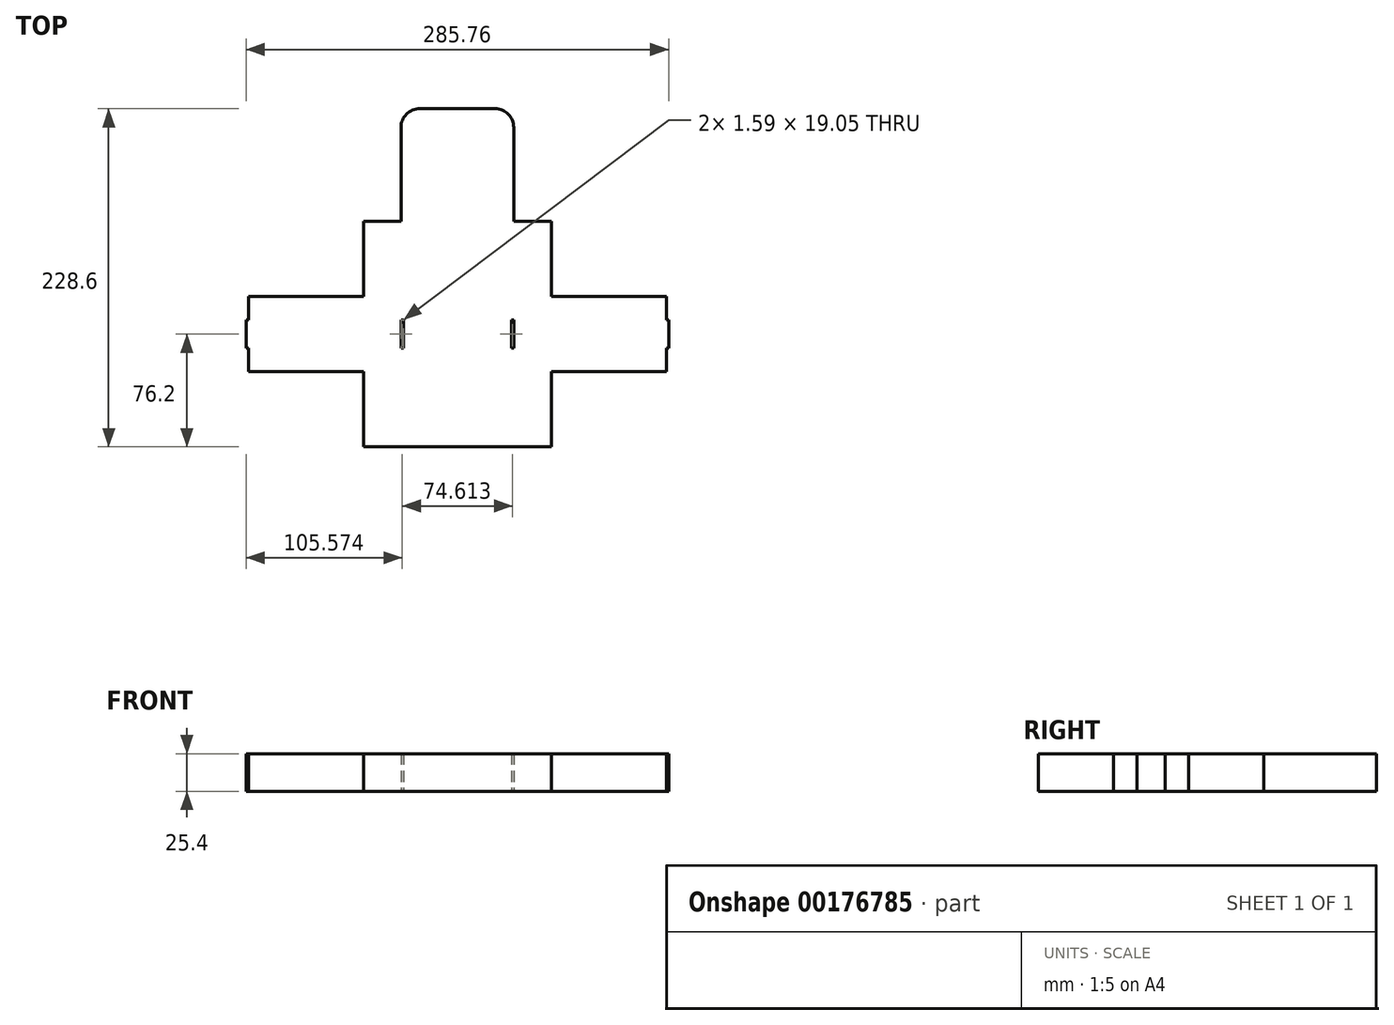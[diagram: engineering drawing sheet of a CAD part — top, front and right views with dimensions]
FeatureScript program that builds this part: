
annotation { "Feature Type Name" : "Feature", "Feature Type Description" : "" }
export const myFeature = defineFeature(function(context is Context, id is Id, definition is map)
    precondition{}
    {
        {
            var Q0;
            Q0=qCreatedBy(makeId("Top.planeOp"),FACE);
            var sketch = newSketch(context, id + "F0", { "sketchPlane" : qUnion([Q0])});
            skLineSegment(sketch, "E0.bottom", {"start": v(38.1, 25.4) * mm, "end": v(-38.1, 25.4) * mm});
            skLineSegment(sketch, "E0.top", {"start": v(38.1, -25.4) * mm, "end": v(-38.1, -25.4) * mm});
            skLineSegment(sketch, "E0.left", {"start": v(38.1, 25.4) * mm, "end": v(38.1, -25.4) * mm});
            skLineSegment(sketch, "E0.right", {"start": v(-38.1, 25.4) * mm, "end": v(-38.1, -25.4) * mm});
            skPoint(sketch, "E0.middle", {"position": v(0, 0) * mm});
            skLineSegment(sketch, "E1", {"start": v(38.1, 25.4) * mm, "end": v(88.9, 25.4) * mm});
            skLineSegment(sketch, "E2", {"start": v(88.9, 25.4) * mm, "end": v(88.9, -25.4) * mm});
            skLineSegment(sketch, "E3", {"start": v(88.9, -25.4) * mm, "end": v(38.1, -25.4) * mm});
            skLineSegment(sketch, "E4", {"start": v(88.9, 25.4) * mm, "end": v(90.49, 25.4) * mm});
            skLineSegment(sketch, "E5", {"start": v(90.49, 25.4) * mm, "end": v(90.49, -25.4) * mm});
            skLineSegment(sketch, "E6", {"start": v(90.49, -25.4) * mm, "end": v(88.9, -25.4) * mm});
            skLineSegment(sketch, "E7", {"start": v(90.49, -25.4) * mm, "end": v(141.29, -25.4) * mm});
            skLineSegment(sketch, "E8", {"start": v(141.29, -25.4) * mm, "end": v(141.29, 25.4) * mm});
            skLineSegment(sketch, "E9", {"start": v(141.29, 25.4) * mm, "end": v(90.49, 25.4) * mm});
            skLineSegment(sketch, "E10", {"start": v(0, 25.4) * mm, "end": v(0, -25.4) * mm, "construction": true});
            skLineSegment(sketch, "E11", {"start": v(-38.1, 0) * mm, "end": v(38.1, 0) * mm, "construction": true});
            skLineSegment(sketch, "E12.MirrorCS", {"start": v(-88.9, -25.4) * mm, "end": v(-38.1, -25.4) * mm});
            skLineSegment(sketch, "E13.MirrorCS", {"start": v(-38.1, 25.4) * mm, "end": v(-88.9, 25.4) * mm});
            skLineSegment(sketch, "E14.MirrorCS", {"start": v(-90.49, -25.4) * mm, "end": v(-88.9, -25.4) * mm});
            skLineSegment(sketch, "E15.MirrorCS", {"start": v(-88.9, 25.4) * mm, "end": v(-90.49, 25.4) * mm});
            skLineSegment(sketch, "E16.MirrorCS", {"start": v(-141.29, 25.4) * mm, "end": v(-90.49, 25.4) * mm});
            skLineSegment(sketch, "E17.MirrorCS", {"start": v(-90.49, -25.4) * mm, "end": v(-141.29, -25.4) * mm});
            skLineSegment(sketch, "E18.MirrorCS", {"start": v(-141.29, -25.4) * mm, "end": v(-141.29, 25.4) * mm});
            skLineSegment(sketch, "E19.MirrorCS", {"start": v(-88.9, 25.4) * mm, "end": v(-88.9, -25.4) * mm});
            skLineSegment(sketch, "E20.MirrorCS", {"start": v(-90.49, 25.4) * mm, "end": v(-90.49, -25.4) * mm});
            skLineSegment(sketch, "E21", {"start": v(-38.1, -25.4) * mm, "end": v(-38.1, -76.2) * mm});
            skLineSegment(sketch, "E22", {"start": v(-38.1, -76.2) * mm, "end": v(38.1, -76.2) * mm});
            skLineSegment(sketch, "E23", {"start": v(38.1, -76.2) * mm, "end": v(38.1, -25.4) * mm});
            skLineSegment(sketch, "E24", {"start": v(-38.1, 25.4) * mm, "end": v(-38.1, 76.2) * mm});
            skLineSegment(sketch, "E25", {"start": v(-38.1, 76.2) * mm, "end": v(38.1, 76.2) * mm});
            skLineSegment(sketch, "E26", {"start": v(38.1, 76.2) * mm, "end": v(38.1, 25.4) * mm});
            skLineSegment(sketch, "E27", {"start": v(38.1, 76.2) * mm, "end": v(38.1, 127) * mm});
            skLineSegment(sketch, "E28", {"start": v(38.1, 127) * mm, "end": v(-38.1, 127) * mm});
            skLineSegment(sketch, "E29", {"start": v(-38.1, 127) * mm, "end": v(-38.1, 76.2) * mm});
            skLineSegment(sketch, "E30", {"start": v(-38.1, 127) * mm, "end": v(-38.1, 139.7) * mm});
            skLineSegment(sketch, "E31", {"start": v(-25.4, 152.4) * mm, "end": v(25.4, 152.4) * mm});
            skLineSegment(sketch, "E32", {"start": v(38.1, 139.7) * mm, "end": v(38.1, 127) * mm});
            skPoint(sketch, "E33.visualSharp", {"position": v(-38.1, 152.4) * mm});
            skArc(sketch, "E33.filletArc", {"start": v(-25.4, 152.4) * mm, "mid": v(-34.38, 148.68) * mm, "end": v(-38.1, 139.7) * mm});
            skPoint(sketch, "E34.visualSharp", {"position": v(38.1, 152.4) * mm});
            skArc(sketch, "E34.filletArc", {"start": v(38.1, 139.7) * mm, "mid": v(34.38, 148.68) * mm, "end": v(25.4, 152.4) * mm});
            skLineSegment(sketch, "E35", {"start": v(-141.29, 9.53) * mm, "end": v(-142.88, 9.53) * mm});
            skLineSegment(sketch, "E36", {"start": v(-142.88, 9.53) * mm, "end": v(-142.88, -9.52) * mm});
            skLineSegment(sketch, "E37", {"start": v(-142.88, -9.52) * mm, "end": v(-141.29, -9.52) * mm});
            skPoint(sketch, "E38", {"position": v(-142.88, 0) * mm});
            skLineSegment(sketch, "E39.bottom", {"start": v(-38.1, 9.53) * mm, "end": v(-36.51, 9.53) * mm});
            skLineSegment(sketch, "E39.top", {"start": v(-38.1, -9.53) * mm, "end": v(-36.51, -9.53) * mm});
            skLineSegment(sketch, "E39.left", {"start": v(-38.1, 9.53) * mm, "end": v(-38.1, -9.53) * mm});
            skLineSegment(sketch, "E39.right", {"start": v(-36.51, 9.52) * mm, "end": v(-36.51, -9.52) * mm});
            skLineSegment(sketch, "E40.MirrorCS", {"start": v(142.88, -9.53) * mm, "end": v(141.29, -9.53) * mm});
            skLineSegment(sketch, "E41.MirrorCS", {"start": v(142.88, 9.52) * mm, "end": v(142.88, -9.52) * mm});
            skLineSegment(sketch, "E42.MirrorCS", {"start": v(141.29, 9.52) * mm, "end": v(142.88, 9.52) * mm});
            skLineSegment(sketch, "E43.MirrorCS", {"start": v(38.1, 9.53) * mm, "end": v(38.1, -9.53) * mm});
            skLineSegment(sketch, "E44.MirrorCS", {"start": v(38.1, 9.52) * mm, "end": v(36.51, 9.52) * mm});
            skLineSegment(sketch, "E45.MirrorCS", {"start": v(38.1, -9.53) * mm, "end": v(36.51, -9.53) * mm});
            skLineSegment(sketch, "E46.MirrorCS", {"start": v(36.51, 9.53) * mm, "end": v(36.51, -9.53) * mm});
            skLineSegment(sketch, "E47", {"start": v(-38.1, -76.2) * mm, "end": v(-63.5, -76.2) * mm});
            skLineSegment(sketch, "E48", {"start": v(-63.5, -76.2) * mm, "end": v(-63.5, -25.4) * mm});
            skLineSegment(sketch, "E49.MirrorCS", {"start": v(38.1, -76.2) * mm, "end": v(63.5, -76.2) * mm});
            skLineSegment(sketch, "E50.MirrorCS", {"start": v(63.5, -76.2) * mm, "end": v(63.5, -25.4) * mm});
            skLineSegment(sketch, "E51.MirrorCS", {"start": v(-63.5, 76.2) * mm, "end": v(-63.5, 25.4) * mm});
            skLineSegment(sketch, "E52.MirrorCS", {"start": v(-38.1, 76.2) * mm, "end": v(-63.5, 76.2) * mm});
            skLineSegment(sketch, "E53.MirrorCS", {"start": v(63.5, 76.2) * mm, "end": v(63.5, 25.4) * mm});
            skLineSegment(sketch, "E54.MirrorCS", {"start": v(38.1, 76.2) * mm, "end": v(63.5, 76.2) * mm});
            skSolve(sketch);
        }
        {
            var Q0;
            Q0 = qSketchRegion(id + "F0", true);
            var Q1;
            {var subQ6=sQuery(id+"F0.wireOp",EDGE,"E0.bottom");Q1=makeQuery(id+"F0.imprint","IMPRINT",FACE,{"disambiguationData":[TD([[makeQuery(id+"F0.imprint","IMPRINT",EDGE,{"derivedFrom":subQ6}),1.0]])]});}
            extrude(context, id + "F1", {"entities" : qUnion([Q0, Q1]), "depth" : 25.4 * mm});
        }
    });
